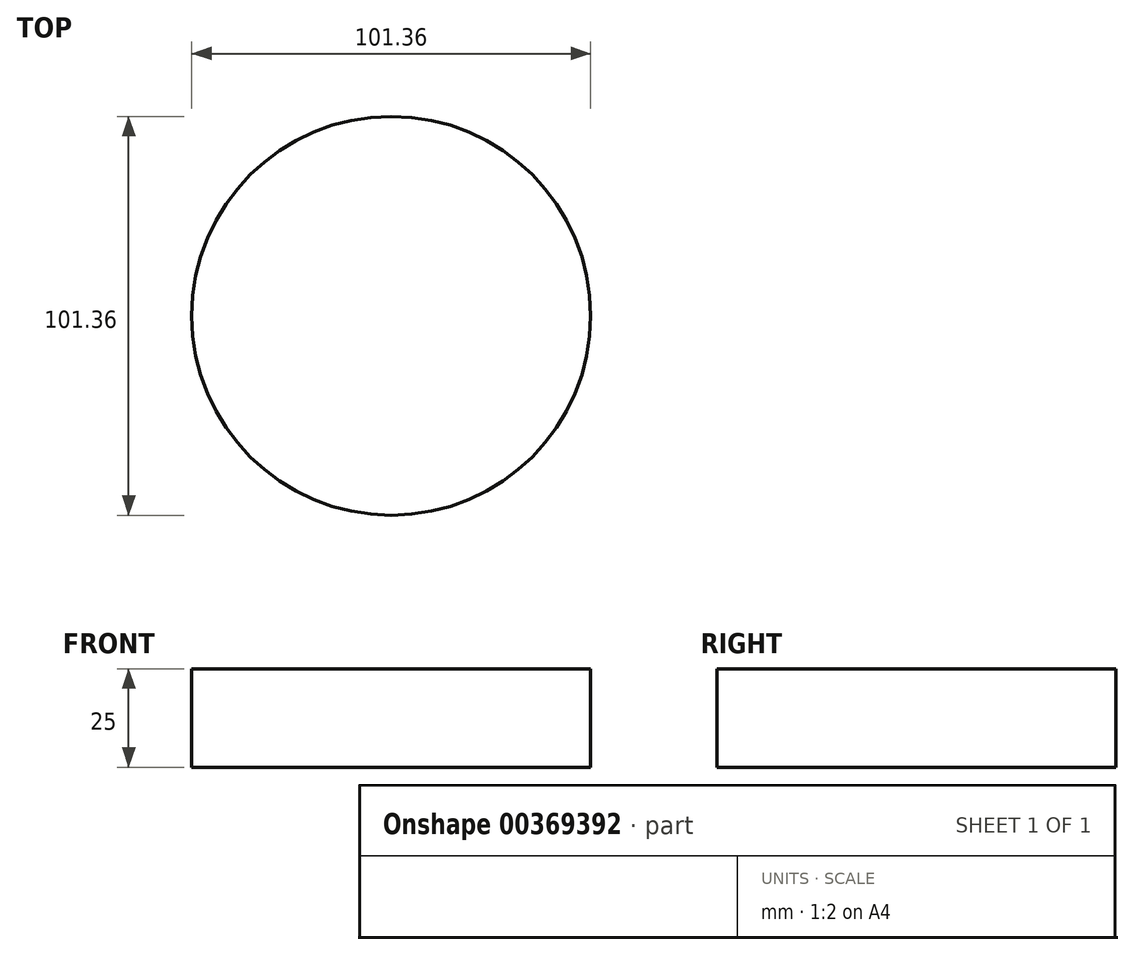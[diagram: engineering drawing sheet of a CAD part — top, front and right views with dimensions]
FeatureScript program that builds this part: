
annotation { "Feature Type Name" : "Feature", "Feature Type Description" : "" }
export const myFeature = defineFeature(function(context is Context, id is Id, definition is map)
    precondition{}
    {
        {
            var Q0;
            Q0=qCreatedBy(makeId("Top.planeOp"),FACE);
            var sketch = newSketch(context, id + "F0", { "sketchPlane" : qUnion([Q0])});
            skCircle(sketch, "E0", {"center": v(0, 0) * mm, "radius": 50.67 * mm});
            skSolve(sketch);
        }
        {
            var Q0;
            Q0=makeQuery(id+"FNvcYfr9Lqj9XMt_0.imprint","IMPRINT",FACE,{"disambiguationData":[TD([[makeQuery(id+"FNvcYfr9Lqj9XMt_0.imprint","IMPRINT",EDGE,{"derivedFrom":sQuery(id+"FNvcYfr9Lqj9XMt_0.wireOp",EDGE,"fTxhzE5y-N2UU-tUj8-n8be-s8B0o2PZ9h2w")}),-1.0]])]});
            var sketch = newSketch(context, id + "F1", { "sketchPlane" : qUnion([Q0])});
            skLineSegment(sketch, "E1", {"start": v(0, 17.62) * mm, "end": v(0, 50.67) * mm});
            skLineSegment(sketch, "E2", {"start": v(0, -17.62) * mm, "end": v(0, -50.67) * mm});
            skLineSegment(sketch, "E3", {"start": v(17.62, 0) * mm, "end": v(50.67, 0) * mm});
            skLineSegment(sketch, "E4", {"start": v(-17.62, 0) * mm, "end": v(-50.67, 0) * mm});
            skSolve(sketch);
        }
        {
            var Q0;
            Q0=qCreatedBy(makeId("Top.planeOp"),FACE);
            var sketch = newSketch(context, id + "F2", { "sketchPlane" : qUnion([Q0])});
            skCircle(sketch, "E5", {"center": v(0, 0) * mm, "radius": 34.15 * mm});
            skSolve(sketch);
        }
        {
            var Q0;
            Q0=qCreatedBy(makeId("Top.planeOp"),FACE);
            var sketch = newSketch(context, id + "F3", { "sketchPlane" : qUnion([Q0])});
            skCircle(sketch, "E6", {"center": v(0, 34.15) * mm, "radius": 12 * mm});
            skCircle(sketch, "E7", {"center": v(-34.15, 0) * mm, "radius": 12 * mm});
            skCircle(sketch, "E8", {"center": v(34.15, 0) * mm, "radius": 12 * mm});
            skCircle(sketch, "E9", {"center": v(0, -34.15) * mm, "radius": 12 * mm});
            skSolve(sketch);
        }
        {
            var Q0;
            Q0=qCreatedBy(makeId("Front.planeOp"),FACE);
            var sketch = newSketch(context, id + "F4", { "sketchPlane" : qUnion([Q0])});
            skLineSegment(sketch, "E10", {"start": v(0, 0) * mm, "end": v(0, 80) * mm});
            skSolve(sketch);
        }
        {
            var Q0;
            Q0=makeQuery(id+"F0.imprint","IMPRINT",FACE,{"disambiguationData":[TD([[makeQuery(id+"F0.imprint","IMPRINT",EDGE,{"derivedFrom":sQuery(id+"F0.wireOp",EDGE,"E0")}),1.0]])]});
            var sketch = newSketch(context, id + "F5", { "sketchPlane" : qUnion([Q0])});
            skCircle(sketch, "E11", {"center": v(-24.15, 24.15) * mm, "radius": 12 * mm});
            skCircle(sketch, "E12", {"center": v(24.16, 24.16) * mm, "radius": 12 * mm});
            skCircle(sketch, "E13", {"center": v(24.15, -24.14) * mm, "radius": 12 * mm});
            skCircle(sketch, "E14", {"center": v(-24.15, -24.15) * mm, "radius": 12 * mm});
            skSolve(sketch);
        }
        {
            var Q0;
            Q0=qSketchRegion(id+"F0",true);
            extrude(context, id + "F6", {"entities" : qUnion([Q0]), "depth" : 25 * mm});
        }
    });
